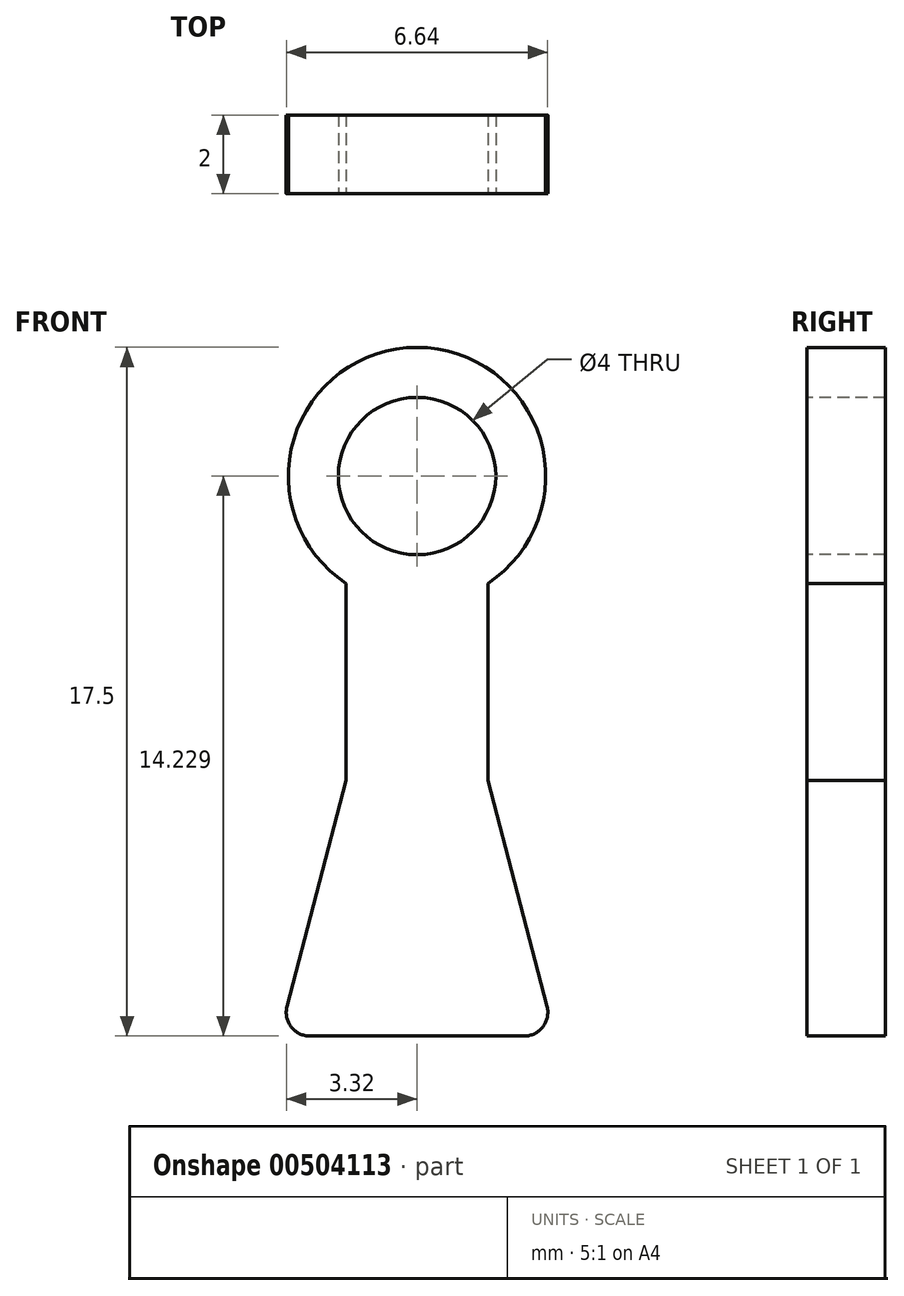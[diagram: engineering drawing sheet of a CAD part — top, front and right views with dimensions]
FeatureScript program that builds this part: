
annotation { "Feature Type Name" : "Feature", "Feature Type Description" : "" }
export const myFeature = defineFeature(function(context is Context, id is Id, definition is map)
    precondition{}
    {
        {
            var Q0;
            Q0=qCreatedBy(makeId("Front.planeOp"),FACE);
            var sketch = newSketch(context, id + "F0", { "sketchPlane" : qUnion([Q0])});
            skLineSegment(sketch, "E0.bottom", {"start": v(-3.5, 9) * mm, "end": v(3.5, 9) * mm});
            skLineSegment(sketch, "E0.top", {"start": v(-3.5, -9) * mm, "end": v(3.5, -9) * mm});
            skLineSegment(sketch, "E0.left", {"start": v(-3.5, 9) * mm, "end": v(-3.5, -9) * mm});
            skLineSegment(sketch, "E0.right", {"start": v(3.5, 9) * mm, "end": v(3.5, -9) * mm});
            skPoint(sketch, "E1", {"position": v(-3.5, 0) * mm});
            skPoint(sketch, "E2", {"position": v(3.5, 0) * mm});
            skPoint(sketch, "E3", {"position": v(0, 9) * mm});
            skPoint(sketch, "E4", {"position": v(0, -9) * mm});
            skLineSegment(sketch, "E5", {"start": v(0, 9) * mm, "end": v(0, -9) * mm, "construction": true});
            skLineSegment(sketch, "E6", {"start": v(3.5, 0) * mm, "end": v(-3.5, 0) * mm, "construction": true});
            skPoint(sketch, "E7", {"position": v(0, 0) * mm});
            skSolve(sketch);
        }
        {
            var Q0;
            Q0=makeQuery(id+"F0.imprint","IMPRINT",FACE,{"disambiguationData":[TD([[makeQuery(id+"F0.imprint","IMPRINT",EDGE,{"derivedFrom":sQuery(id+"F0.wireOp",EDGE,"E0.bottom")}),-1.0]])]});
            var sketch = newSketch(context, id + "F1", { "sketchPlane" : qUnion([Q0])});
            skLineSegment(sketch, "E8", {"start": v(3.5, -9) * mm, "end": v(1.8, -2.5) * mm});
            skLineSegment(sketch, "E9", {"start": v(1.8, -2.5) * mm, "end": v(1.8, 2.5) * mm});
            skLineSegment(sketch, "E10", {"start": v(0, 16.64) * mm, "end": v(0, -16.62) * mm, "construction": true});
            skLineSegment(sketch, "E11.MirrorCS", {"start": v(-1.8, -2.5) * mm, "end": v(-1.8, 2.5) * mm});
            skLineSegment(sketch, "E12.MirrorCS", {"start": v(-3.5, -9) * mm, "end": v(-1.8, -2.5) * mm});
            skLineSegment(sketch, "E13", {"start": v(-3.5, -9) * mm, "end": v(3.5, -9) * mm});
            skPoint(sketch, "E14", {"position": v(1.8, 0) * mm});
            skArc(sketch, "E15", {"start": v(1.8, 2.5) * mm, "mid": v(0, 8.5) * mm, "end": v(-1.8, 2.5) * mm});
            skSolve(sketch);
        }
        {
            var Q0;
            Q0 = qSketchRegion(id + "F0", true);
            extrude(context, id + "F2", {"entities" : qUnion([Q0]), "depth" : 2 * mm});
        }
        {
            var Q0;
            Q0 = qSketchRegion(id + "F1", true);
            extrude(context, id + "F3", {"entities" : qUnion([Q0]), "operationType" : NewBodyOperationType.INTERSECT, "endBound" : BoundingType.SYMMETRIC, "oppositeDirection" : true, "depth" : 25 * mm});
        }
        {
            var Q0;
            {var subQ0=sQuery(id+"F0.wireOp",EDGE,"E0.right");Q0=makeQuery(id+"F3.boolean.opBoolean","MERGE",EDGE,{"derivedFrom":[makeQuery(id+"F2.opExtrude","SWEPT_EDGE",EDGE,{"disambiguationData":[OSD([sQuery(id+"F0.wireOp",EDGE,"E0.top"),subQ0])]}),makeQuery(id+"F3.boolean.toolComplement.opBoolean","COPY",EDGE,{"derivedFrom":makeQuery(id+"F3.opExtrude","SWEPT_EDGE",EDGE,{"disambiguationData":[OSD([subQ0,sQuery(id+"F1.wireOp",EDGE,"E8"),sQuery(id+"F1.wireOp",EDGE,"E13")])]})})]});}
            fillet(context, id + "F4", {"entities" : qUnion([Q0]), "radius" : 0.6 * mm, "tangentPropagation" : true, "allowEdgeOverflow" : false});
        }
        {
            var Q0;
            {var subQ0=sQuery(id+"F0.wireOp",EDGE,"E0.left");Q0=makeQuery(id+"F3.boolean.opBoolean","MERGE",EDGE,{"derivedFrom":[makeQuery(id+"F2.opExtrude","SWEPT_EDGE",EDGE,{"disambiguationData":[OSD([sQuery(id+"F0.wireOp",EDGE,"E0.top"),subQ0])]}),makeQuery(id+"F3.boolean.toolComplement.opBoolean","COPY",EDGE,{"derivedFrom":makeQuery(id+"F3.opExtrude","SWEPT_EDGE",EDGE,{"disambiguationData":[OSD([subQ0,sQuery(id+"F1.wireOp",EDGE,"E12.MirrorCS"),sQuery(id+"F1.wireOp",EDGE,"E13")])]})})]});}
            fillet(context, id + "F5", {"entities" : qUnion([Q0]), "radius" : 0.6 * mm, "tangentPropagation" : true, "allowEdgeOverflow" : false});
        }
        {
            var Q0;
            Q0=makeQuery(id+"F2.opExtrude","CAP_FACE",FACE,{"disambiguationData":[OSD([sQuery(id+"F0.wireOp",EDGE,"E0.bottom"),sQuery(id+"F0.wireOp",EDGE,"E0.top"),sQuery(id+"F0.wireOp",EDGE,"E0.left"),sQuery(id+"F0.wireOp",EDGE,"E0.right")])],"isStart":false});
            var sketch = newSketch(context, id + "F6", { "sketchPlane" : qUnion([Q0])});
            skCircle(sketch, "E16", {"center": v(0, 5.23) * mm, "radius": 2 * mm});
            skSolve(sketch);
        }
        {
            var Q0;
            Q0=makeQuery(id+"F6.imprint","IMPRINT",FACE,{"disambiguationData":[TD([[makeQuery(id+"F6.imprint","IMPRINT",EDGE,{"derivedFrom":sQuery(id+"F6.wireOp",EDGE,"E16")}),1.0]])]});
            var Q1;
            Q1=sQuery(id+"F6.wireOp",EDGE,"E16");
            extrude(context, id + "F7", {"entities" : qUnion([Q0]), "operationType" : NewBodyOperationType.REMOVE, "surfaceEntities" : qUnion([Q1]), "oppositeDirection" : true, "depth" : 25 * mm});
        }
    });
